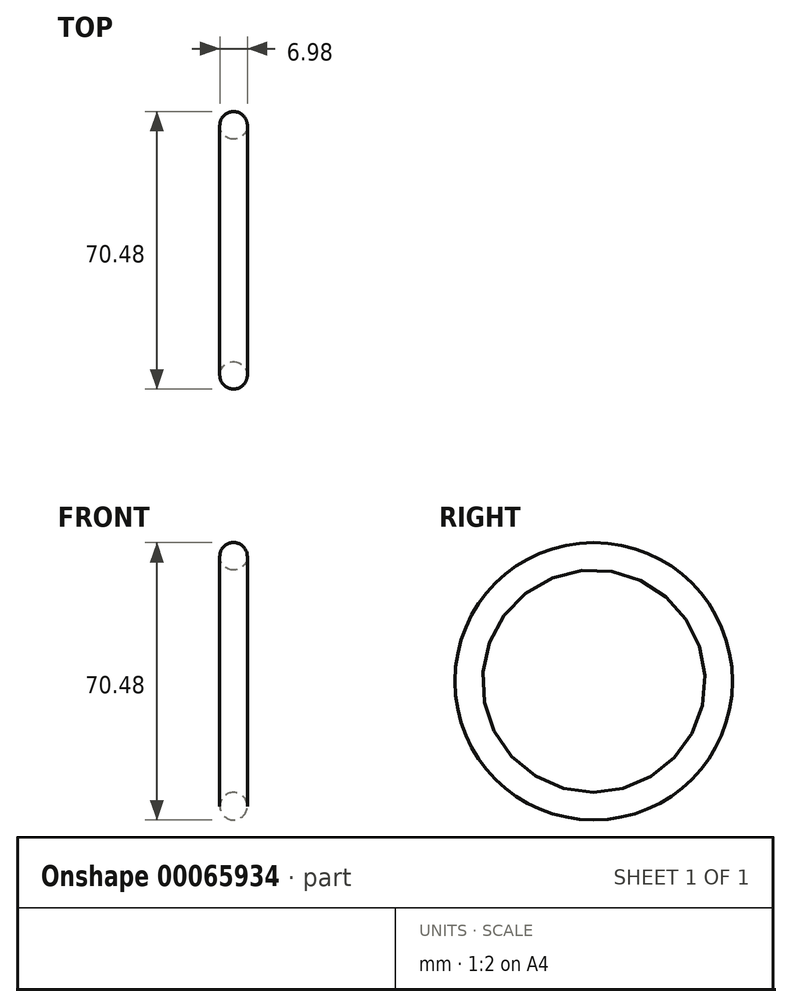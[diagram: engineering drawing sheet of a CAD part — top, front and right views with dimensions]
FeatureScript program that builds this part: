
annotation { "Feature Type Name" : "Feature", "Feature Type Description" : "" }
export const myFeature = defineFeature(function(context is Context, id is Id, definition is map)
    precondition{}
    {
        {
            var Q0;
            Q0=qCreatedBy(makeId("Front.planeOp"),FACE);
            var sketch = newSketch(context, id + "F0", { "sketchPlane" : qUnion([Q0])});
            skLineSegment(sketch, "E0", {"start": v(0, 0) * mm, "end": v(-6.06, 0) * mm, "construction": true});
            skCircle(sketch, "E1", {"center": v(0, 31.75) * mm, "radius": 3.5 * mm});
            skSolve(sketch);
        }
        {
            var Q0;
            Q0=makeQuery(id+"F0.imprint","IMPRINT",FACE,{"disambiguationData":[TD([[makeQuery(id+"F0.imprint","IMPRINT",EDGE,{"derivedFrom":sQuery(id+"F0.wireOp",EDGE,"E1")}),1.0]])]});
            var Q1;
            Q1=sQuery(id+"F0.wireOp",EDGE,"E0");
            revolve(context, id + "F1", {"entities" : qUnion([Q0]), "axis" : qUnion([Q1]), "revolveType" : RevolveType.FULL});
        }
    });
